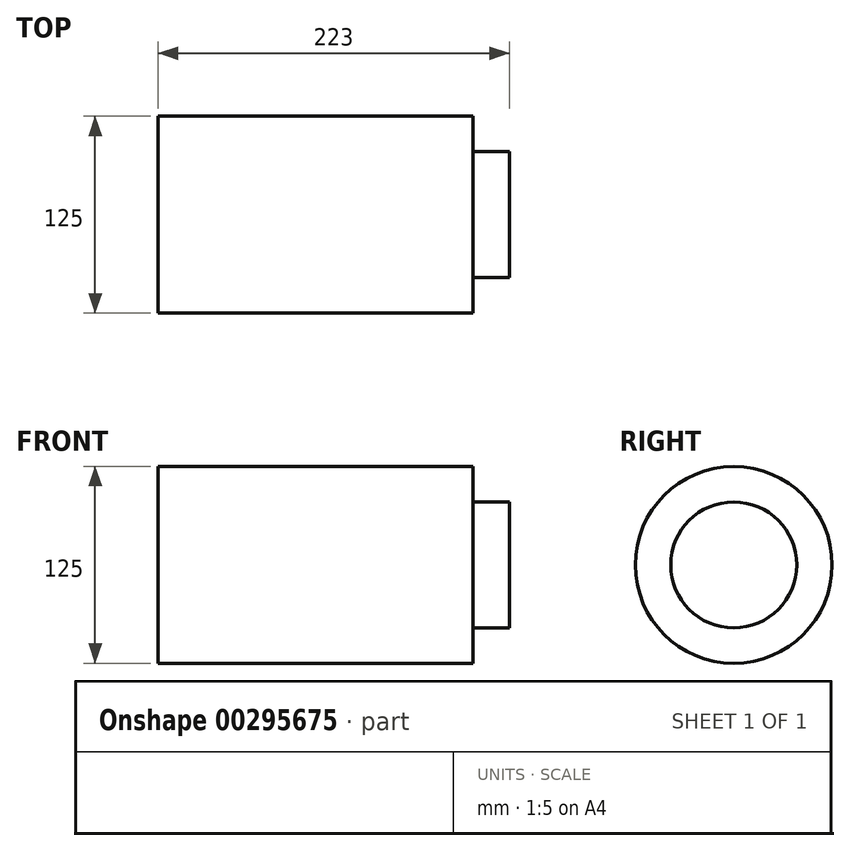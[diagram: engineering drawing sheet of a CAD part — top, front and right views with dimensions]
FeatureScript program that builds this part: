
annotation { "Feature Type Name" : "Feature", "Feature Type Description" : "" }
export const myFeature = defineFeature(function(context is Context, id is Id, definition is map)
    precondition{}
    {
        {
            var Q0;
            Q0=qCreatedBy(makeId("Right.planeOp"),FACE);
            var sketch = newSketch(context, id + "F0", { "sketchPlane" : qUnion([Q0])});
            skCircle(sketch, "E0", {"center": v(0, 0) * mm, "radius": 62.5 * mm});
            skCircle(sketch, "E1", {"center": v(0, 0) * mm, "radius": 40 * mm});
            skSolve(sketch);
        }
        {
            var Q0;
            Q0=makeQuery(id+"F0.imprint","IMPRINT",FACE,{"disambiguationData":[TD([[makeQuery(id+"F0.imprint","IMPRINT",EDGE,{"derivedFrom":sQuery(id+"F0.wireOp",EDGE,"E1")}),1.0]])]});
            var Q1;
            Q1=makeQuery(id+"F0.imprint","IMPRINT",FACE,{"disambiguationData":[TD([[makeQuery(id+"F0.imprint","IMPRINT",EDGE,{"derivedFrom":sQuery(id+"F0.wireOp",EDGE,"E0")}),1.0]])]});
            extrude(context, id + "F1", {"entities" : qUnion([Q0, Q1]), "oppositeDirection" : true, "depth" : 200 * mm});
        }
        {
            var Q0;
            Q0=makeQuery(id+"F0.imprint","IMPRINT",FACE,{"disambiguationData":[TD([[makeQuery(id+"F0.imprint","IMPRINT",EDGE,{"derivedFrom":sQuery(id+"F0.wireOp",EDGE,"E1")}),1.0]])]});
            extrude(context, id + "F2", {"entities" : qUnion([Q0]), "operationType" : NewBodyOperationType.ADD, "depth" : 23 * mm});
        }
    });
